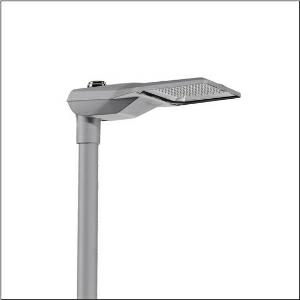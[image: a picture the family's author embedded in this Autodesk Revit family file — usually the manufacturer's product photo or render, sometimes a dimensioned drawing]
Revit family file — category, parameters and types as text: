
# Revit family: streetlight_sl_21_midi___st0_8a_5xe7c47n08nb_23c8
name_source: partatom
category: Lighting Fixtures
units: mm (PartAtom-declared; Revit-internal decimal feet)

## family parameters
Cut with Voids When Loaded = No
Host = Face
Light Source = No
Part Type = Normal
Room Calculation Point = No
Round Connector Dimension = Use Diameter
Shared = No

## types (1)
- --- (1 x LED, 23710 lm, 151.2 W, 4000K)
    Apparent Load = 151 VA
    CIE Flux Codes = 41 75 97 100 100
    Color Rendering = 70
    Color Temperature = 4000K
    Default Elevation = 1800 mm
    Description = Streetlight SL 21 midi, mast luminaire, primary light control with lens, of PMMA, primary optical cover: cover, of toughened safety glass, transparent, light distribution: ST0.8a, light emission: direct distribution, primary light characteristic: asymmetric, installation type: side-entry, LED, 3G 2.5mm², High Power LED, rated luminous flux: 23.710lm, luminous efficacy: 157lm/W, light colour: 740, colour temperature: 4000K, control gear: NEMA (7pin), control: overheat protection, pre-setting: linear dimming characteristic, constant luminous flux control, time-dependent luminous flux control, flexible luminous flux parameterisation, mains connection: 220..240V, AC, 50/60Hz, connection cable pre-assembled, cable length: 12,5m, wiring characteristics: H05VV-F, start of lifetime: 151W, end of service life: 157W, reduction: 70W, luminaire housing, of diecast aluminium (EN AC-44300), powder-coated, SITECO metallic grey (DB 702S), corrosivity category C5 high according to DIN EN ISO 12944, multi-level sealing system, sealing non-destructively replaceable, inclination adjustable: 0°, 5°, 10°, 15°, length: 644mm, width: 335mm, height: 110mm, spigot size: 42mm (side-entry), mounting height: 4..8m, protection rating (complete): IP66, insulation class (complete): insulation class I (protective earthing), certification: CE, ENEC, ENEC+, VDE, impact resistance: IK10, permissible operating ambient temperature for outdoor applications: -40..+50°C, standard-compliant lighting for roads and squares, packaging unit: 1 piece

Light Distribution: ST0.8a
    Height = 111 mm
    Lamp = 1 x LED
    Lamp Light Flux = 23710 lm
    Lamp Power = 151.2 W
    Lamp count = 1
    Length = 644 mm
    Luminous efficacy = 157 lm/W
    Manufacturer = Siteco
    ModVariant = No
    Model = 5XE7C47N08NB
    Number of Poles = 1
    OnlyDefault = Yes
    Power Factor = 1
    Product Name = Streetlight SL 21 midi | ST0.8a
    Product group = mast luminaire | pylon top
    ProductGroupID = 6100
    Protection Class = Protection class I
    Protection Degree = IP 66
    RLX_Detail_Level = 1
    RLX_Emergency_Light_Flux = 0 lm
    RLX_Emergency_Type = 0
    RLX_Emergency_Type_DB = No
    RlxData = <blob elided: 26605 chars, md5=e5ba3f4f>
    Socket = socket
    Standby Power = 0 W
    System Light Flux = 23710 lm
    System Power = 151 W
    Type Comments = factory setting: luminous flux: 100 % | dim-lin: 254 | 802 mA
    Type Image = l_1294377.jpg
    URL = http://relux.com
    VarID = @adj_133331
    Voltage = 0 V
    Weight = 0.00 kg
    Width = 336 mm

## geometry (parser evidence)
native form markers: Blend x4, Sweep x9
no freeform markers — native parametric forms only
